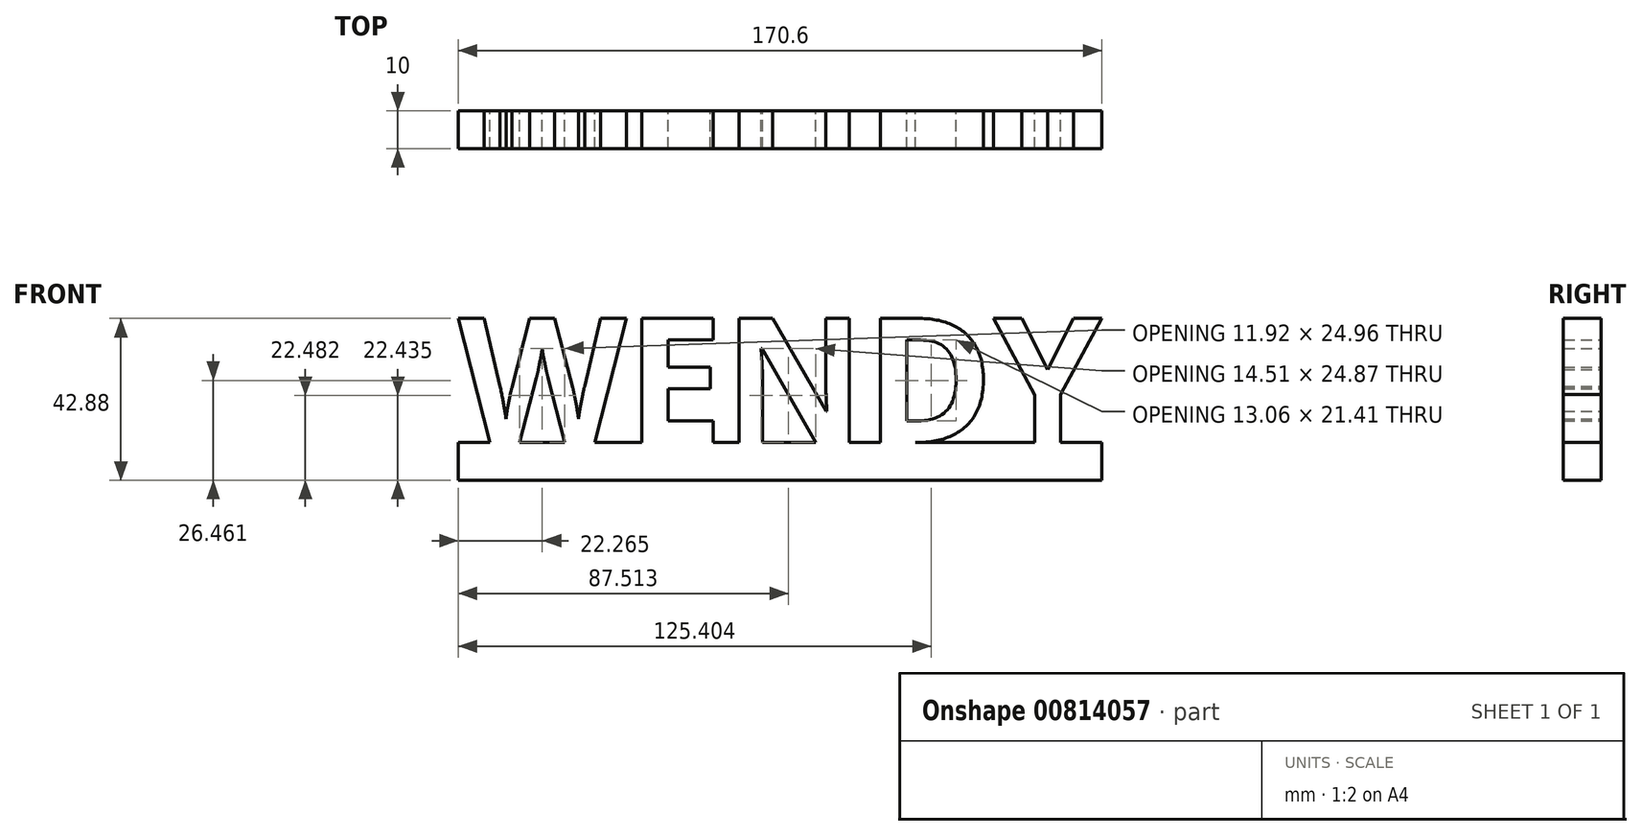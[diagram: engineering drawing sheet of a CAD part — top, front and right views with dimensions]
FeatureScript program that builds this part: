
annotation { "Feature Type Name" : "Feature", "Feature Type Description" : "" }
export const myFeature = defineFeature(function(context is Context, id is Id, definition is map)
    precondition{}
    {
        {
            var Q0;
            Q0=qCreatedBy(makeId("Front.planeOp"),FACE);
            var sketch = newSketch(context, id + "F0", { "sketchPlane" : qUnion([Q0])});
            skText(sketch, "E0", { "text": "WENDY", "fontName": "OpenSans-Bold.ttf"});
            const initialGuessF0  = {"E0": [-0.0745, 0, 1, 0, 0.03316]};
            skSetInitialGuess(sketch, initialGuessF0);
            skSolve(sketch);
        }
        {
            var Q0;
            Q0=qSketchRegion(id+"F0",true);
            extrude(context, id + "F1", {"entities" : qUnion([Q0]), "depth" : 10 * mm, "offsetDistance" : 25 * mm});
        }
        {
            var Q0;
            Q0=makeQuery(id+"F1.opExtrude","SWEPT_FACE",FACE,{"disambiguationData":[OSD([sQuery(id+"F0.wireOp",EDGE,"E0.sketch_text.stroke-24")])]});
            var sketch = newSketch(context, id + "F2", { "sketchPlane" : qUnion([Q0])});
            skLineSegment(sketch, "E1.bottom", {"start": v(96.08, 0) * mm, "end": v(-74.5, 0) * mm});
            skLineSegment(sketch, "E1.top", {"start": v(96.08, 10) * mm, "end": v(-74.5, 10) * mm});
            skLineSegment(sketch, "E1.left", {"start": v(96.08, 0) * mm, "end": v(96.08, 10) * mm});
            skLineSegment(sketch, "E1.right", {"start": v(-74.5, 0) * mm, "end": v(-74.5, 10) * mm});
            skSolve(sketch);
        }
        {
            var Q0;
            Q0 = qSketchRegion(id + "F2", true);
            extrude(context, id + "F3", {"entities" : qUnion([Q0]), "operationType" : NewBodyOperationType.ADD, "depth" : 10 * mm, "offsetDistance" : 25 * mm});
        }
    });
